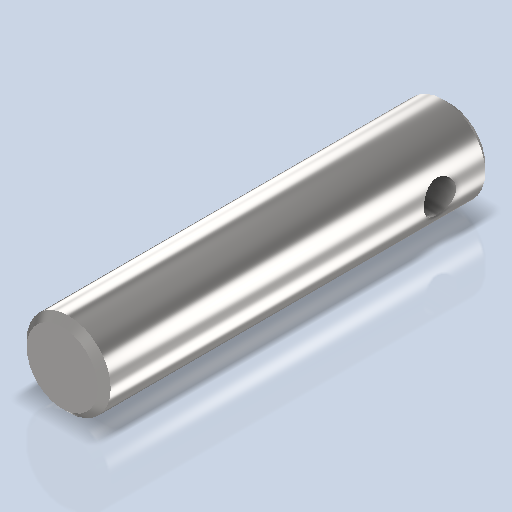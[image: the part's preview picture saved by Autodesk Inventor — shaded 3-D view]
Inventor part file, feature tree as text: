
AUTODESK INVENTOR PART (.ipt)
format: ipt  version: 2024.2 (Build 282272000, 272)  size: 264,704 bytes
history: native  units: mm
features: sketch x2, extrude x1, chamfer x1, plane x1, hole x1
ambient origin geometry x8: Origin, YZ Plane, XZ Plane, XY Plane, X Axis, Y Axis, Z Axis, Center Point
bodies: Volumenkörper1 (feature_tree)
feature tree (6):
  extrude  "Extrusion1"  Depth=30.0mm TaperAngle=0.0deg
  chamfer  "Fasen1"  Distance=0.5mm Angle=45.0deg
  plane  "Arbeitsebene1"
  hole  "Bohrung1"  [1 undecoded]
  sketch  "Skizze1"  dims[d0=6.5mm d1=30.0mm d2=0.0mm d3=0.5mm d4=2.0mm d5=45.0deg]
  sketch  "Skizze2"  dims[d6=3.25mm d8=4.0mm d9=2.5mm d10=6.0mm d11=4.0mm d12=2.0mm d13=90.0deg d14=8.0mm d15=0.0mm]
note: 1 required parameter value undecoded (feature->parameter linkage not recoverable at this tier; creation-order binding heuristic only, values carry confidence <= 0.55)
